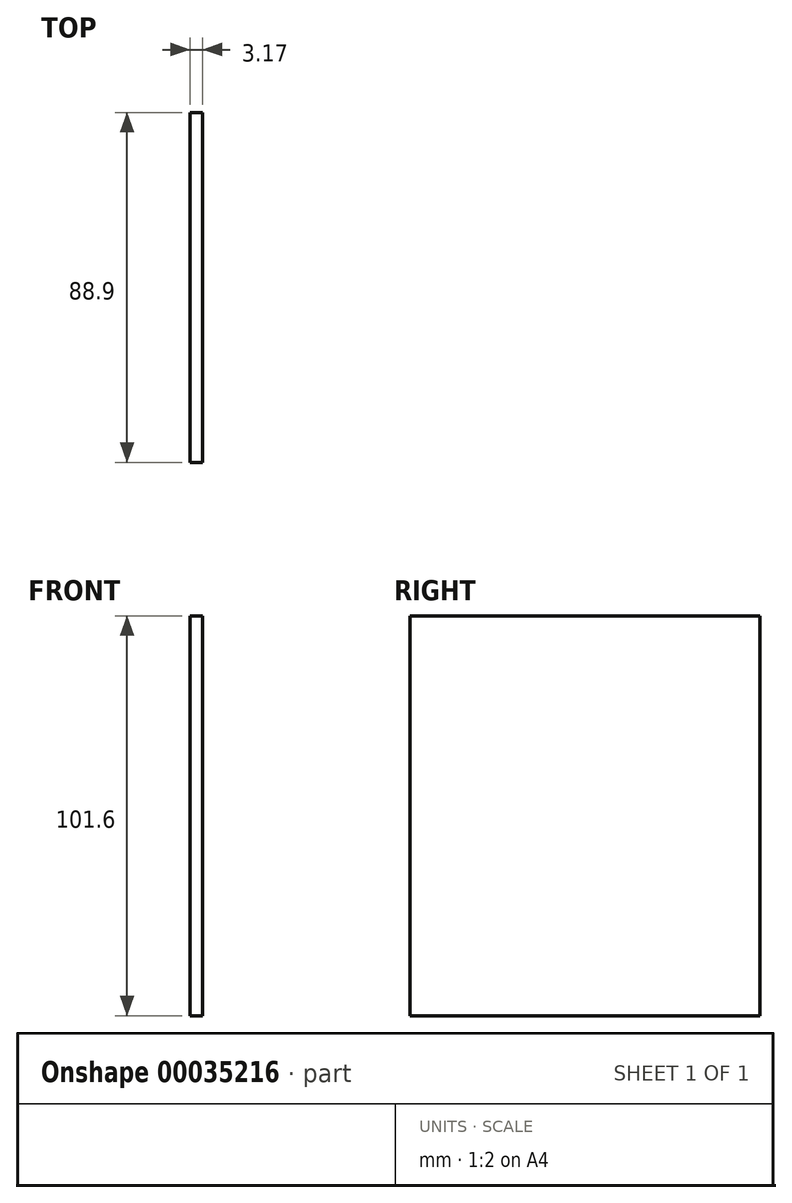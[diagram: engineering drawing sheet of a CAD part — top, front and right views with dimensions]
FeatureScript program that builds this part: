
annotation { "Feature Type Name" : "Feature", "Feature Type Description" : "" }
export const myFeature = defineFeature(function(context is Context, id is Id, definition is map)
    precondition{}
    {
        {
            var Q0;
            Q0=qCreatedBy(makeId("Right.planeOp"),FACE);
            var sketch = newSketch(context, id + "F0", { "sketchPlane" : qUnion([Q0])});
            skLineSegment(sketch, "E0.bottom", {"start": v(-37.92, 39.57) * mm, "end": v(50.98, 39.57) * mm});
            skLineSegment(sketch, "E0.top", {"start": v(-37.92, -62.03) * mm, "end": v(50.98, -62.03) * mm});
            skLineSegment(sketch, "E0.left", {"start": v(-37.92, 39.57) * mm, "end": v(-37.92, -62.03) * mm});
            skLineSegment(sketch, "E0.right", {"start": v(50.98, 39.57) * mm, "end": v(50.98, -62.03) * mm});
            skSolve(sketch);
        }
        {
            var Q0;
            Q0=makeQuery(id+"F0.imprint","IMPRINT",FACE,{"disambiguationData":[TD([[makeQuery(id+"F0.imprint","IMPRINT",EDGE,{"derivedFrom":sQuery(id+"F0.wireOp",EDGE,"E0.bottom")}),-1.0]])]});
            extrude(context, id + "F1", {"entities" : qUnion([Q0]), "depth" : 3.17 * mm});
        }
    });
